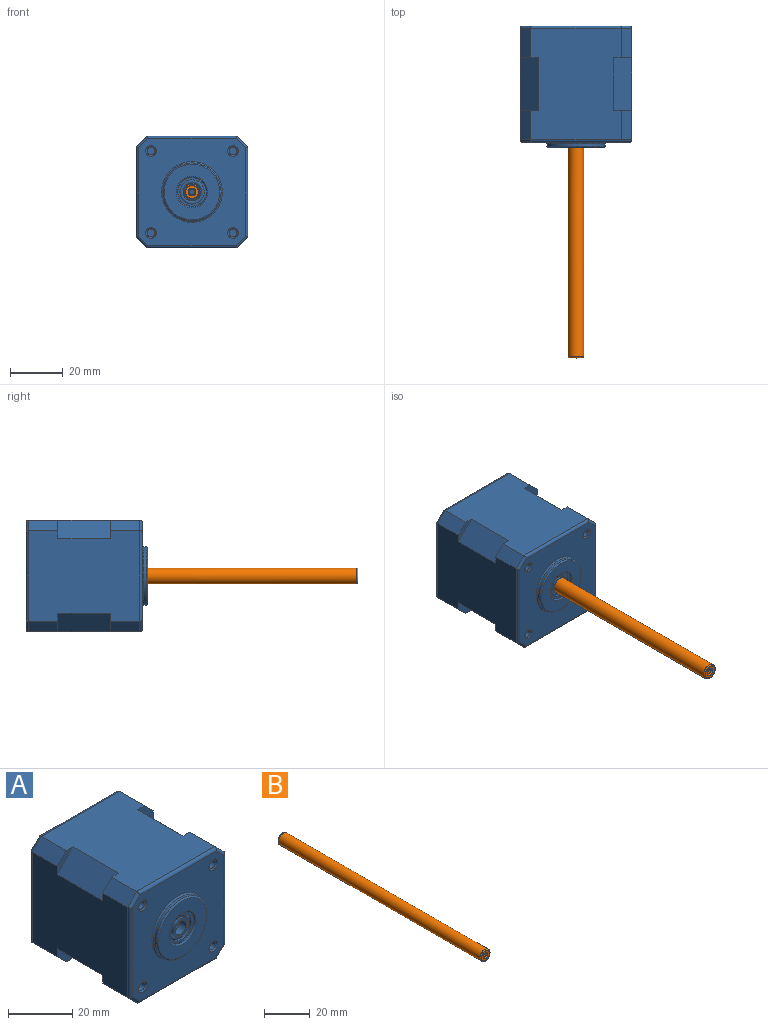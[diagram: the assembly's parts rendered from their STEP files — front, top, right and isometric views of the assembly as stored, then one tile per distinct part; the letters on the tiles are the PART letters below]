
ASSEMBLY  parts=2 mates=1
PART A: 190 faces, bbox 42.3x46x42.3 mm
  f0: torus R=5.35mm, axis (0,-1,0), area 8.1mm2, adj f14,f20
  f1: torus R=5.35mm, axis (0,-1,0), area 8.1mm2, adj f13,f19
  f2: cylinder r=4.6mm len=9.2mm, axis (0,-1,0), area 24mm2, adj f4,f14
  f3: cylinder r=4.6mm len=9.2mm, axis (0,-1,0), area 24mm2, adj f10,f13
  f4: torus R=4mm, axis (0,1,0), area 33mm2, adj f2,f8
  f5: torus R=2.65mm, axis (0,-1,0), area 3.8mm2, adj f6,f12
  f6: cylinder r=2.5mm len=5mm, axis (0,-1,0), area 42.4mm2, adj f5,f7
  f7: torus R=2.65mm, axis (0,-1,0), area 3.8mm2, adj f6,f11
  f8: cylinder r=3.4mm len=6.8mm, axis (0,-1,0), area 17.7mm2, adj f4,f12
  f9: cylinder r=3.4mm len=6.8mm, axis (0,-1,0), area 17.7mm2, adj f10,f11
  f10: torus R=4mm, axis (0,1,0), area 33mm2, adj f3,f9
  f11: plane 6.8x6.8mm, normal (0,-1,0), area 14.3mm2, adj f7,f9
  f12: plane 6.8x6.8mm, normal (0,1,0), area 14.3mm2, adj f5,f8
  f13: plane 10.7x10.7mm, normal (0,-1,0), area 23.4mm2, adj f1,f3
  f14: plane 10.7x10.7mm, normal (0,1,0), area 23.4mm2, adj f0,f2
  f15: plane 5x5mm, normal (0,1,0), area 19.6mm2, adj f16
  f16: cylinder r=2.5mm len=5mm, axis (0,1,0), area 78.5mm2, adj f15,f17
  f17: plane 9x9mm, normal (0,1,0), area 44mm2, adj f16,f18
  f18: torus R=4.5mm, axis (0,1,0), area 50.7mm2, adj f17,f19
  f19: cylinder r=5.5mm len=11mm, axis (0,1,0), area 8.6mm2, adj f1,f18
  f20: cylinder r=5.5mm len=11mm, axis (0,1,0), area 1.8mm2, adj f0,f159
  f21: torus R=5.35mm, axis (0,1,0), area 8.1mm2, adj f35,f41
  f22: torus R=5.35mm, axis (0,1,0), area 8.1mm2, adj f34,f40
  f23: cylinder r=4.6mm len=9.2mm, axis (0,1,0), area 24mm2, adj f25,f35
  f24: cylinder r=4.6mm len=9.2mm, axis (0,1,0), area 24mm2, adj f31,f34
  f25: torus R=4mm, axis (0,-1,0), area 33mm2, adj f23,f29
  f26: torus R=2.65mm, axis (0,1,0), area 3.8mm2, adj f27,f33
  f27: cylinder r=2.5mm len=5mm, axis (0,1,0), area 42.4mm2, adj f26,f28
  f28: torus R=2.65mm, axis (0,1,0), area 3.8mm2, adj f27,f32
  f29: cylinder r=3.4mm len=6.8mm, axis (0,1,0), area 17.7mm2, adj f25,f33
  f30: cylinder r=3.4mm len=6.8mm, axis (0,1,0), area 17.7mm2, adj f31,f32
  f31: torus R=4mm, axis (0,-1,0), area 33mm2, adj f24,f30
  f32: plane 6.8x6.8mm, normal (0,1,0), area 14.3mm2, adj f28,f30
  f33: plane 6.8x6.8mm, normal (0,-1,0), area 14.3mm2, adj f26,f29
  f34: plane 10.7x10.7mm, normal (0,1,0), area 23.4mm2, adj f22,f24
  f35: plane 10.7x10.7mm, normal (0,-1,0), area 23.4mm2, adj f21,f23
  f36: plane 5x5mm, normal (0,-1,0), area 19.6mm2, adj f37
  f37: cylinder r=2.5mm len=5mm, axis (0,-1,0), area 78.5mm2, adj f36,f38
  f38: plane 10x10mm, normal (0,-1,0), area 58.9mm2, adj f37,f39
  f39: torus R=5mm, axis (0,-1,0), area 26.2mm2, adj f38,f40
  f40: cylinder r=5.5mm len=11mm, axis (0,-1,0), area 100.7mm2, adj f22,f39
  f41: cylinder r=5.5mm len=11mm, axis (0,-1,0), area 13.3mm2, adj f21,f116
  f42: torus R=2.44mm, axis (0,1,0), area 6.3mm2, adj f43,f44
  f43: cylinder r=2.8mm len=5.6mm, axis (0,1,0), area 23.7mm2, adj f42,f177
  f44: sphere r=5mm, area 20.2mm2, adj f42,f45,f46,f47,f48,f49,f50,f52
  f45: plane 1.74x0.93mm, normal (-0.88,0.1,0.47), area 0.9mm2, adj f44,f49,f54
  f46: plane 1.74x1.08mm, normal (-0.88,0.1,0.47), area 0.9mm2, adj f44,f50,f53
  f47: plane 1.74x1.08mm, normal (0.88,0.1,-0.47), area 0.9mm2, adj f44,f49,f56
  f48: plane 1.74x0.93mm, normal (0.88,0.1,-0.47), area 0.9mm2, adj f44,f50,f57
  f49: plane 1.59x1.26mm, normal (-0.38,0.58,-0.72), area 1mm2, adj f44,f45,f47,f51
  f50: plane 1.59x1.26mm, normal (0.38,0.58,0.72), area 1mm2, adj f44,f46,f48,f51
  f51: plane 0.5x0.5mm, normal (0,1,0), area 0.1mm2, adj f49,f50,f52,f55
  f52: plane 1.6x1.26mm, normal (-0.72,0.58,0.38), area 1mm2, adj f44,f51,f53,f54
  f53: plane 1.73x0.92mm, normal (0.47,0.1,0.88), area 0.9mm2, adj f44,f46,f52
  f54: plane 1.73x1.08mm, normal (-0.47,0.1,-0.88), area 0.9mm2, adj f44,f45,f52
  f55: plane 1.6x1.26mm, normal (0.72,0.58,-0.38), area 1mm2, adj f44,f51,f56,f57
  f56: plane 1.73x0.92mm, normal (-0.47,0.1,-0.88), area 0.9mm2, adj f44,f47,f55
  f57: plane 1.73x1.08mm, normal (0.47,0.1,0.88), area 0.9mm2, adj f44,f48,f55
  f58: cylinder r=2.8mm len=5.6mm, axis (0,1,0), area 23mm2, adj f59,f153
  f59: torus R=2.44mm, axis (0,1,0), area 6.3mm2, adj f58,f60
  f60: sphere r=5mm, area 20.2mm2, adj f59,f61,f62,f63,f64,f65,f66,f68
  f61: plane 1.74x1.1mm, normal (-0.91,0.1,-0.4), area 0.9mm2, adj f60,f65,f70
  f62: plane 1.74x0.97mm, normal (-0.91,0.1,-0.4), area 0.9mm2, adj f60,f66,f69
  f63: plane 1.74x0.97mm, normal (0.91,0.1,0.4), area 0.9mm2, adj f60,f65,f72
  f64: plane 1.74x1.1mm, normal (0.91,0.1,0.4), area 0.9mm2, adj f60,f66,f73
  f65: plane 1.59x1.26mm, normal (0.33,0.58,-0.74), area 1mm2, adj f60,f61,f63,f67
  f66: plane 1.59x1.26mm, normal (-0.33,0.58,0.74), area 1mm2, adj f60,f62,f64,f67
  f67: plane 0.49x0.49mm, normal (0,1,0), area 0.1mm2, adj f65,f66,f68,f71
  f68: plane 1.6x1.27mm, normal (-0.74,0.58,-0.33), area 1mm2, adj f60,f67,f69,f70
  f69: plane 1.73x1.1mm, normal (-0.4,0.1,0.91), area 0.9mm2, adj f60,f62,f68
  f70: plane 1.73x0.97mm, normal (0.4,0.1,-0.91), area 0.9mm2, adj f60,f61,f68
  f71: plane 1.6x1.27mm, normal (0.74,0.58,0.33), area 1mm2, adj f60,f67,f72,f73
  f72: plane 1.73x1.1mm, normal (0.4,0.1,-0.91), area 0.9mm2, adj f60,f63,f71
  f73: plane 1.73x0.97mm, normal (-0.4,0.1,0.91), area 0.9mm2, adj f60,f64,f71
  f74: cylinder r=2.8mm len=5.6mm, axis (0,1,0), area 23mm2, adj f75,f151
  f75: torus R=2.44mm, axis (0,1,0), area 6.3mm2, adj f74,f76
  f76: sphere r=5mm, area 20.2mm2, adj f75,f77,f78,f79,f80,f81,f82,f84
  f77: plane 1.74x0.89mm, normal (-0.85,0.1,0.51), area 0.9mm2, adj f76,f81,f86
  f78: plane 1.74x1.06mm, normal (-0.85,0.1,0.51), area 0.9mm2, adj f76,f82,f85
  f79: plane 1.74x1.06mm, normal (0.85,0.1,-0.51), area 0.9mm2, adj f76,f81,f88
  f80: plane 1.74x0.89mm, normal (0.85,0.1,-0.51), area 0.9mm2, adj f76,f82,f89
  f81: plane 1.59x1.25mm, normal (-0.42,0.58,-0.7), area 1mm2, adj f76,f77,f79,f83
  f82: plane 1.59x1.25mm, normal (0.42,0.58,0.7), area 1mm2, adj f76,f78,f80,f83
  f83: plane 0.51x0.51mm, normal (0,1,0), area 0.1mm2, adj f81,f82,f84,f87
  f84: plane 1.6x1.26mm, normal (-0.7,0.58,0.42), area 1mm2, adj f76,f83,f85,f86
  f85: plane 1.73x0.89mm, normal (0.51,0.1,0.85), area 0.9mm2, adj f76,f78,f84
  f86: plane 1.73x1.06mm, normal (-0.51,0.1,-0.85), area 0.9mm2, adj f76,f77,f84
  f87: plane 1.6x1.26mm, normal (0.7,0.58,-0.42), area 1mm2, adj f76,f83,f88,f89
  f88: plane 1.73x0.89mm, normal (-0.51,0.1,-0.85), area 0.9mm2, adj f76,f79,f87
  f89: plane 1.73x1.06mm, normal (0.51,0.1,0.85), area 0.9mm2, adj f76,f80,f87
  f90: cylinder r=2.8mm len=5.6mm, axis (0,1,0), area 23mm2, adj f91,f149
  f91: torus R=2.44mm, axis (0,1,0), area 6.3mm2, adj f90,f92
  f92: sphere r=5mm, area 20.2mm2, adj f91,f93,f94,f95,f96,f97,f98,f100
  f93: plane 1.74x0.94mm, normal (-0.89,0.1,0.44), area 0.9mm2, adj f92,f97,f102
  f94: plane 1.74x1.09mm, normal (-0.89,0.1,0.44), area 0.9mm2, adj f92,f98,f101
  f95: plane 1.74x1.09mm, normal (0.89,0.1,-0.44), area 0.9mm2, adj f92,f97,f104
  f96: plane 1.74x0.94mm, normal (0.89,0.1,-0.44), area 0.9mm2, adj f92,f98,f105
  f97: plane 1.59x1.26mm, normal (-0.36,0.58,-0.73), area 1mm2, adj f92,f93,f95,f99
  f98: plane 1.59x1.26mm, normal (0.36,0.58,0.73), area 1mm2, adj f92,f94,f96,f99
  f99: plane 0.5x0.5mm, normal (0,1,0), area 0.1mm2, adj f97,f98,f100,f103
  f100: plane 1.6x1.27mm, normal (-0.73,0.58,0.36), area 1mm2, adj f92,f99,f101,f102
  f101: plane 1.73x0.94mm, normal (0.44,0.1,0.89), area 0.9mm2, adj f92,f94,f100
  f102: plane 1.73x1.09mm, normal (-0.44,0.1,-0.89), area 0.9mm2, adj f92,f93,f100
  f103: plane 1.6x1.27mm, normal (0.73,0.58,-0.36), area 1mm2, adj f92,f99,f104,f105
  f104: plane 1.73x0.94mm, normal (-0.44,0.1,-0.89), area 0.9mm2, adj f92,f95,f103
  f105: plane 1.73x1.09mm, normal (0.44,0.1,0.89), area 0.9mm2, adj f92,f96,f103
  f106: torus R=2mm, axis (0,-1,0), area 8.3mm2, adj f113,f118
  f107: torus R=2mm, axis (0,-1,0), area 8.3mm2, adj f112,f118
  f108: torus R=2mm, axis (0,-1,0), area 8.3mm2, adj f111,f118
  f109: torus R=2mm, axis (0,-1,0), area 8.3mm2, adj f110,f118
  f110: cylinder r=1.5mm len=4mm, axis (0,-1,0), area 37.7mm2, adj f109,f143
  f111: cylinder r=1.5mm len=4mm, axis (0,-1,0), area 37.7mm2, adj f108,f142
  f112: cylinder r=1.5mm len=4mm, axis (0,-1,0), area 37.7mm2, adj f107,f141
  f113: cylinder r=1.5mm len=4mm, axis (0,-1,0), area 37.7mm2, adj f106,f140
  f114: torus R=10.5mm, axis (0,-1,0), area 53.4mm2, adj f117,f131
  f115: torus R=11.5mm, axis (0,-1,0), area 55.2mm2, adj f117,f118
  f116: torus R=6mm, axis (0,-1,0), area 28mm2, adj f41,f131
  f117: cylinder r=11mm len=22mm, axis (0,1,0), area 69.1mm2, adj f114,f115
  f118: plane 40.3x40.3mm, normal (0,-1,0), area 1135mm2, adj f106,f107,f108,f109,f115,f132,f133,f134
  f119: plane 7x7mm, normal (0,1,0), area 16.5mm2, adj f122,f123,f124,f144
  f120: plane 7x7mm, normal (0,1,0), area 16.5mm2, adj f122,f128,f129,f145
  f121: plane 7x7mm, normal (0,1,0), area 16.5mm2, adj f126,f127,f128,f146
  f122: plane 42x34.3mm, normal (0,0,1), area 1320.6mm2, adj f119,f120,f123,f129,f134,f144,f145,f160
  f123: plane 11x4mm, normal (0.71,0,0.71), area 62.2mm2, adj f119,f122,f124,f132
  f124: plane 42x34.3mm, normal (1,0,0), area 1320.6mm2, adj f119,f123,f125,f130,f133,f144,f147,f160
  f125: plane 11x4mm, normal (0.71,0,-0.71), area 62.2mm2, adj f124,f126,f130,f135
  f126: plane 42x34.3mm, normal (0,0,-1), area 1320.6mm2, adj f121,f125,f127,f130,f137,f146,f147,f161
  f127: plane 11x4mm, normal (-0.71,0,-0.71), area 62.2mm2, adj f121,f126,f128,f139
  f128: plane 42x34.3mm, normal (-1,0,0), area 1320.6mm2, adj f120,f121,f127,f129,f138,f145,f146,f162
  f129: plane 11x4mm, normal (-0.71,0,0.71), area 62.2mm2, adj f120,f122,f128,f136
  f130: plane 7x7mm, normal (0,1,0), area 16.5mm2, adj f124,f125,f126,f147
  f131: plane 21x21mm, normal (0,-1,0), area 233.3mm2, adj f114,f116
  f132: cylinder r=1mm len=4.71mm, axis (-0.71,0,0.71), area 8.4mm2, adj f118,f123,f133,f134
  f133: cylinder r=1mm len=34.3mm, axis (0,0,1), area 53.4mm2, adj f118,f124,f132,f135
  f134: cylinder r=1mm len=34.3mm, axis (-1,0,0), area 53.4mm2, adj f118,f122,f132,f136
  f135: cylinder r=1mm len=4.71mm, axis (0.71,0,0.71), area 8.4mm2, adj f118,f125,f133,f137
  f136: cylinder r=1mm len=4.71mm, axis (-0.71,0,-0.71), area 8.4mm2, adj f118,f129,f134,f138
  f137: cylinder r=1mm len=34.3mm, axis (1,0,0), area 53.4mm2, adj f118,f126,f135,f139
  f138: cylinder r=1mm len=34.3mm, axis (0,0,-1), area 53.4mm2, adj f118,f128,f136,f139
  f139: cylinder r=1mm len=4.71mm, axis (0.71,0,-0.71), area 8.4mm2, adj f118,f127,f137,f138
  f140: plane 3x3mm, normal (0,-1,0), area 7.1mm2, adj f113
  f141: plane 3x3mm, normal (0,-1,0), area 7.1mm2, adj f112
  f142: plane 3x3mm, normal (0,-1,0), area 7.1mm2, adj f111
  f143: plane 3x3mm, normal (0,-1,0), area 7.1mm2, adj f110
  f144: plane 20x7mm, normal (0.71,0,0.71), area 198mm2, adj f119,f122,f124,f160
  f145: plane 20x7mm, normal (-0.71,0,0.71), area 198mm2, adj f120,f122,f128,f167
  f146: plane 20x7mm, normal (-0.71,0,-0.71), area 198mm2, adj f121,f126,f128,f162
  f147: plane 20x7mm, normal (0.71,0,-0.71), area 198mm2, adj f124,f126,f130,f161
  f148: torus R=3.6mm, axis (0,-1,0), area 16.2mm2, adj f158,f168
  f149: torus R=2.6mm, axis (0,1,0), area 10.9mm2, adj f90,f158
  f150: torus R=3.6mm, axis (0,-1,0), area 16.2mm2, adj f157,f168
  f151: torus R=2.6mm, axis (0,1,0), area 10.9mm2, adj f74,f157
  f152: torus R=3.6mm, axis (0,-1,0), area 16.2mm2, adj f156,f168
  f153: torus R=2.6mm, axis (0,1,0), area 10.9mm2, adj f58,f156
  f154: torus R=3.6mm, axis (0,-1,0), area 16.2mm2, adj f155,f168
  f155: cylinder r=3.1mm len=6.2mm, axis (0,1,0), area 48.7mm2, adj f154,f177
  f156: cylinder r=3.1mm len=6.2mm, axis (0,1,0), area 39mm2, adj f152,f153
  f157: cylinder r=3.1mm len=6.2mm, axis (0,1,0), area 39mm2, adj f150,f151
  f158: cylinder r=3.1mm len=6.2mm, axis (0,1,0), area 39mm2, adj f148,f149
  f159: torus R=6.5mm, axis (0,-1,0), area 57.9mm2, adj f20,f168
  f160: plane 7x7mm, normal (0,-1,0), area 16.5mm2, adj f122,f124,f144,f165
  f161: plane 7x7mm, normal (0,-1,0), area 16.5mm2, adj f124,f126,f147,f164
  f162: plane 7x7mm, normal (0,-1,0), area 16.5mm2, adj f126,f128,f146,f163
  f163: plane 11x4mm, normal (-0.71,0,-0.71), area 62.2mm2, adj f126,f128,f162,f173
  f164: plane 11x4mm, normal (0.71,0,-0.71), area 62.2mm2, adj f124,f126,f161,f169
  f165: plane 11x4mm, normal (0.71,0,0.71), area 62.2mm2, adj f122,f124,f160,f172
  f166: plane 11x4mm, normal (-0.71,0,0.71), area 62.2mm2, adj f122,f128,f167,f176
  f167: plane 7x7mm, normal (0,-1,0), area 16.5mm2, adj f122,f128,f145,f166
  f168: plane 40.3x40.3mm, normal (0,1,0), area 1305.2mm2, adj f148,f150,f152,f154,f159,f169,f170,f171
  f169: cylinder r=1mm len=4.71mm, axis (0.71,0,0.71), area 8.4mm2, adj f164,f168,f170,f171
  f170: cylinder r=1mm len=34.3mm, axis (0,0,1), area 53.4mm2, adj f124,f168,f169,f172
  f171: cylinder r=1mm len=34.3mm, axis (1,0,0), area 53.4mm2, adj f126,f168,f169,f173
  f172: cylinder r=1mm len=4.71mm, axis (-0.71,0,0.71), area 8.4mm2, adj f165,f168,f170,f174
  f173: cylinder r=1mm len=4.71mm, axis (0.71,0,-0.71), area 8.4mm2, adj f163,f168,f171,f175
  f174: cylinder r=1mm len=34.3mm, axis (-1,0,0), area 53.4mm2, adj f122,f168,f172,f176
  f175: cylinder r=1mm len=34.3mm, axis (0,0,-1), area 53.4mm2, adj f128,f168,f173,f176
  f176: cylinder r=1mm len=4.71mm, axis (-0.71,0,-0.71), area 8.4mm2, adj f166,f168,f174,f175
  f177: plane 6.2x6.2mm, normal (0,1,0), area 5.6mm2, adj f43,f155
  f178: plane 3x3mm, normal (0,1,0), area 7.1mm2, adj f179
  f179: cylinder r=1.5mm len=3mm, axis (0,1,0), area 18.8mm2, adj f178,f180
  f180: plane 3x3mm, normal (0,-1,0), area 7.1mm2, adj f179
  f181: plane 3x3mm, normal (0,1,0), area 7.1mm2, adj f182
  f182: cylinder r=1.5mm len=3mm, axis (0,1,0), area 18.8mm2, adj f181,f183
  f183: plane 3x3mm, normal (0,-1,0), area 7.1mm2, adj f182
  f184: plane 3x3mm, normal (0,1,0), area 7.1mm2, adj f185
  f185: cylinder r=1.5mm len=3mm, axis (0,1,0), area 18.8mm2, adj f184,f186
  f186: plane 3x3mm, normal (0,-1,0), area 7.1mm2, adj f185
  f187: plane 3x3mm, normal (0,1,0), area 7.1mm2, adj f188
  f188: cylinder r=1.5mm len=3mm, axis (0,1,0), area 18.8mm2, adj f187,f189
  f189: plane 3x3mm, normal (0,-1,0), area 7.1mm2, adj f188
PART B: 8 faces, bbox 6.7x125x6.7 mm
  f0: cylinder r=1mm len=124mm, axis (0,-1,0), area 779.1mm2, adj f4,f5
  f1: cylinder r=3mm len=124mm, axis (0,-1,0), area 2337.3mm2, adj f6,f7
  f2: plane 5.01x5.01mm, normal (0,1,0), area 12.6mm2, adj f4,f6
  f3: plane 5.01x5.01mm, normal (0,-1,0), area 12.6mm2, adj f5,f7
  f4: bspline ~3x3mm, area 6mm2, adj f0,f2
  f5: bspline ~3x3mm, area 6mm2, adj f0,f3
  f6: bspline ~6.65x6.65mm, area 14.4mm2, adj f1,f2
  f7: bspline ~6.65x6.65mm, area 14.4mm2, adj f1,f3
PLACE A t=(-23.9,-18.84,-0.17)mm
PLACE B t=(-34.3,-144.39,4.44)mm
MATE revolute B.f1 <-> A.f0  axis (0,-1,0) through (-34.3,-19.89,4.44)mm
